# Revit family: Shower-Base-STERLING-GUARD-72301100_1
name_source: partatom
category: Plumbing Fixtures
revit_build: Autodesk Revit 2017 (Build: 20160225_1515(x64)
units: mm (PartAtom-declared; Revit-internal decimal feet)

## family parameters
Cut with Voids When Loaded = No
Host = Face
OmniClass Number = 23.31.17.15
OmniClass Title = Shower Enclosure Bases
Part Type = Normal
Room Calculation Point = No
Round Connector Dimension = Use Diameter
Shared = No

## types (2) — shared parameters
ADA Compliant = No
Assembly Code = D2010700
CW Connection = No
Cold Water Inlet = Cold Water Inlet
Date Modified = 07/27/2020
Default Elevation = 0"
Description = 36inch x 34 inch Shower Base
Drain Included = No
Flow Rate = 0 GPM
HW Connection = No
Height = 4 3/16"
Hot Water Inlet = Hot Water Inlet
Length = 36"
Manufacturer = STERLING Co.
Master Format 2014 = 22 41 23
Master Format 2014 Name = Residential Showers
Material = Vikrell
Pressure = 0.00 psi
Product Documentation Link = https://resources.kohler.com
Product Name = GUARD
Product Page URL = http://www.sterlingplumbing.com
URL = https://www.sterlingplumbing.com
Vent Connection = No
Waste Connection = Yes
Waste Water Outlet = Waste Water Outlet
WaterSense Certified = No
Width = 34"

## per-type parameters (varying)
| type | Finish | Model | Type |
| 96-Biscuit | Sterling-Vikrell-96-Biscuit | 72301100-96 | 2 |
| 0-White | Sterling-Vikrell-0-White | 72301100-0 | 1 |

## geometry (parser evidence)
native form markers: Sweep x3
no freeform markers — native parametric forms only
